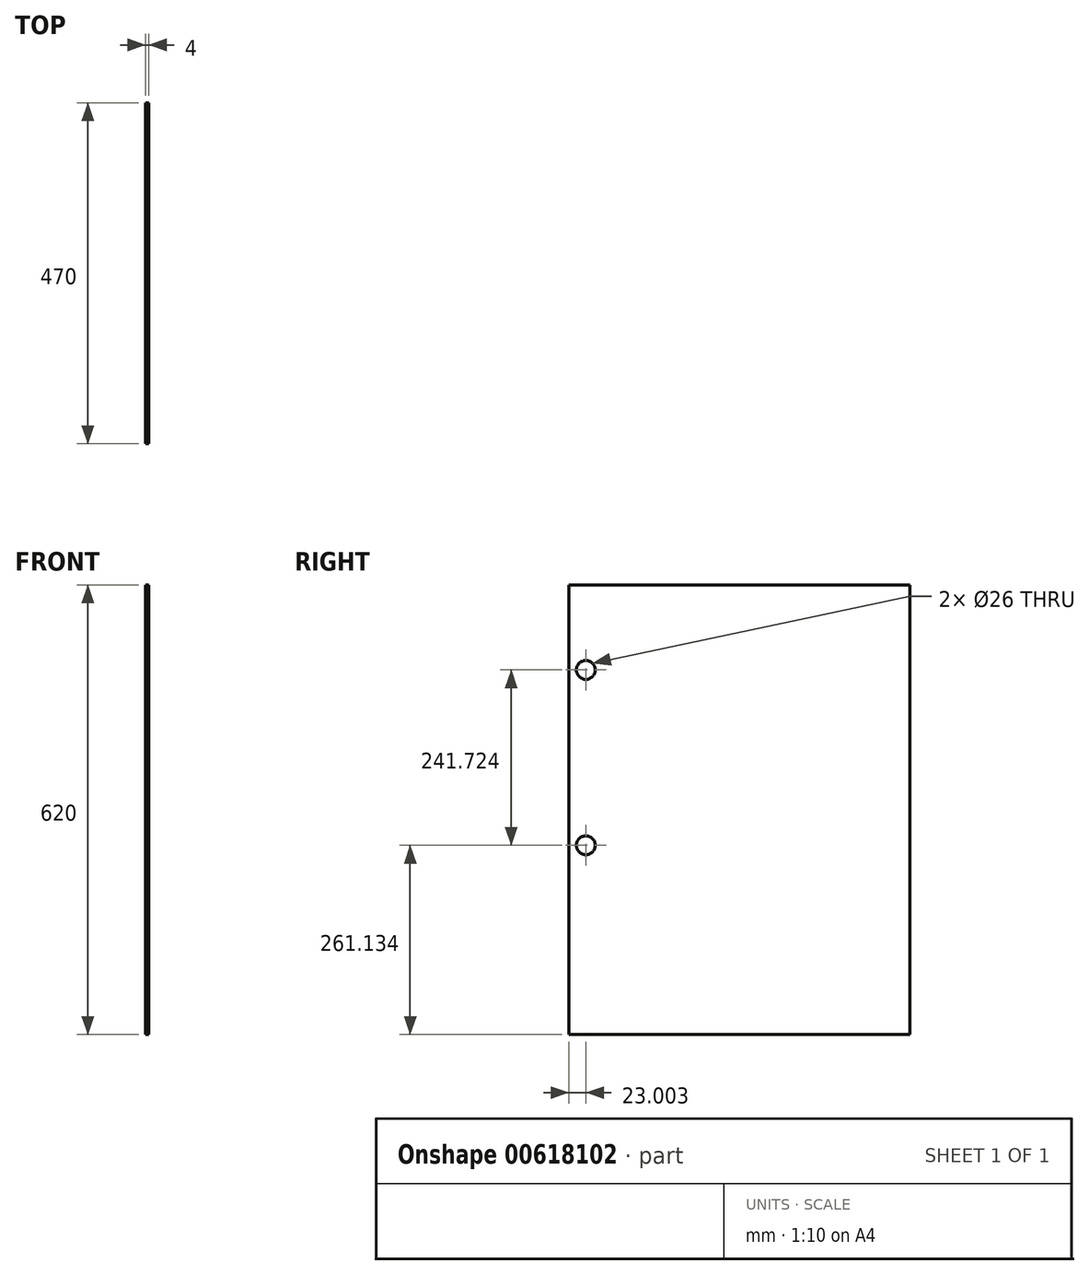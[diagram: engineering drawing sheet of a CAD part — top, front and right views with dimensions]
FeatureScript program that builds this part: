
annotation { "Feature Type Name" : "Feature", "Feature Type Description" : "" }
export const myFeature = defineFeature(function(context is Context, id is Id, definition is map)
    precondition{}
    {
        {
            var Q0;
            Q0=qCreatedBy(makeId("Right.planeOp"),FACE);
            var sketch = newSketch(context, id + "F0", { "sketchPlane" : qUnion([Q0])});
            skLineSegment(sketch, "E0.bottom", {"start": v(-8.8, 560.05) * mm, "end": v(461.2, 560.05) * mm});
            skLineSegment(sketch, "E0.top", {"start": v(-8.8, -59.95) * mm, "end": v(461.2, -59.95) * mm});
            skLineSegment(sketch, "E0.left", {"start": v(-8.8, 560.05) * mm, "end": v(-8.8, -59.95) * mm});
            skLineSegment(sketch, "E0.right", {"start": v(461.2, 560.05) * mm, "end": v(461.2, -59.95) * mm});
            skCircle(sketch, "E1", {"center": v(14.2, 442.9) * mm, "radius": 13 * mm});
            skCircle(sketch, "E2", {"center": v(14.2, 201.18) * mm, "radius": 13 * mm});
            skSolve(sketch);
        }
        {
            var Q0;
            Q0=makeQuery(id+"F0.imprint","IMPRINT",FACE,{"disambiguationData":[TD([[makeQuery(id+"F0.imprint","IMPRINT",EDGE,{"derivedFrom":sQuery(id+"F0.wireOp",EDGE,"E0.bottom")}),-1.0]])]});
            extrude(context, id + "F1", {"entities" : qUnion([Q0]), "depth" : 4 * mm, "offsetDistance" : 25 * mm});
        }
    });
